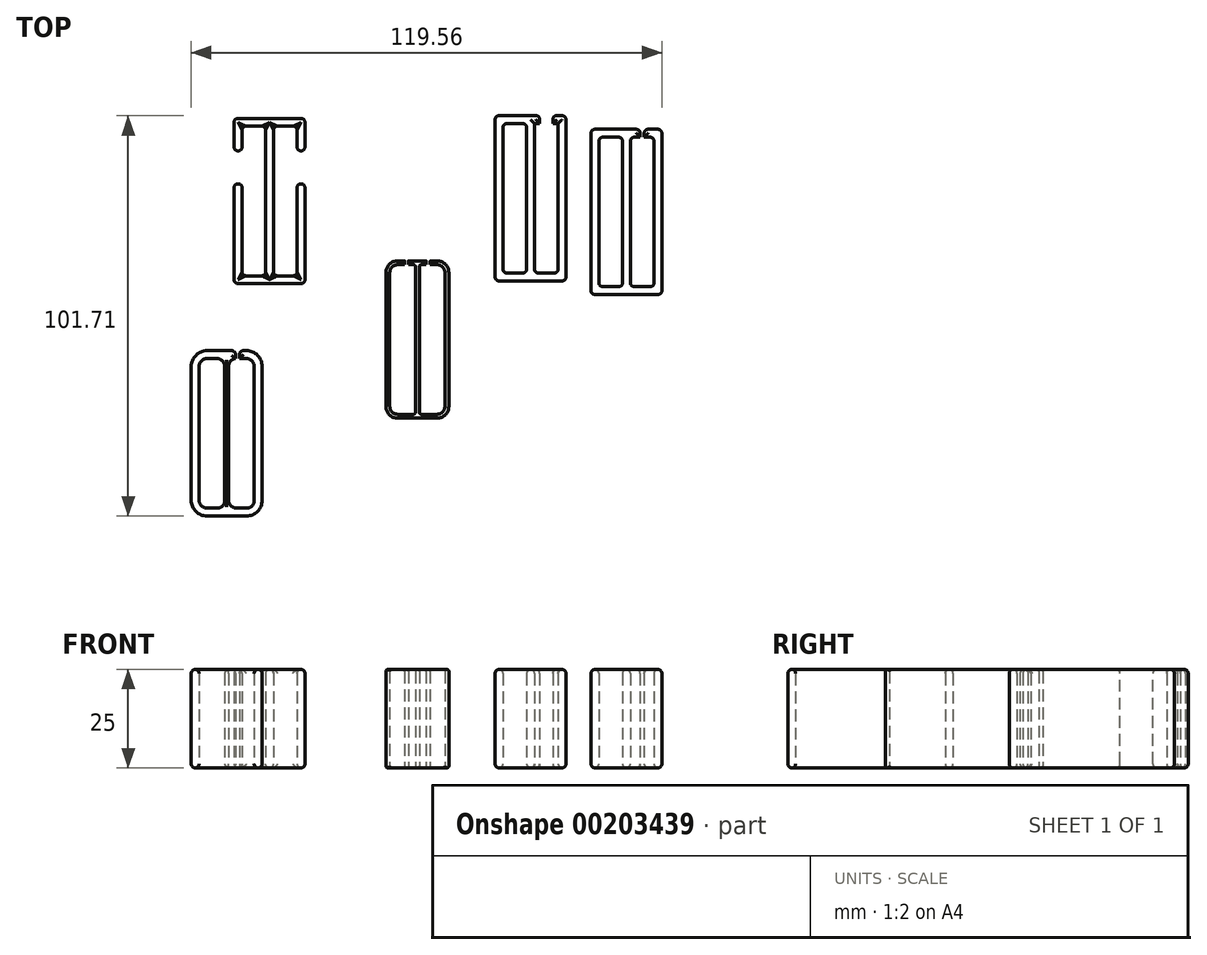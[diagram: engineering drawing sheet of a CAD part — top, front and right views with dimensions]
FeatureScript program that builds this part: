
annotation { "Feature Type Name" : "Feature", "Feature Type Description" : "" }
export const myFeature = defineFeature(function(context is Context, id is Id, definition is map)
    precondition{}
    {
        {
            var Q0;
            Q0=qCreatedBy(makeId("Top.planeOp"),FACE);
            var sketch = newSketch(context, id + "F0", { "sketchPlane" : qUnion([Q0])});
            skLineSegment(sketch, "E0", {"start": v(-46.96, 45) * mm, "end": v(-46.96, 53.26) * mm});
            skLineSegment(sketch, "E1", {"start": v(-46.96, 53.26) * mm, "end": v(-28.96, 53.26) * mm});
            skLineSegment(sketch, "E2", {"start": v(-28.96, 53.26) * mm, "end": v(-28.96, 45) * mm});
            skLineSegment(sketch, "E3", {"start": v(-37.96, 53.26) * mm, "end": v(-37.96, 11.26) * mm});
            skLineSegment(sketch, "E4", {"start": v(-37.96, 11.26) * mm, "end": v(-46.96, 11.26) * mm});
            skLineSegment(sketch, "E5", {"start": v(-46.96, 11.26) * mm, "end": v(-46.96, 36.63) * mm});
            skLineSegment(sketch, "E6", {"start": v(-37.96, 11.26) * mm, "end": v(-28.96, 11.26) * mm});
            skLineSegment(sketch, "E7", {"start": v(-28.96, 11.26) * mm, "end": v(-28.96, 36.63) * mm});
            skLineSegment(sketch, "E8.0", {"start": v(-30.96, 51.26) * mm, "end": v(-30.96, 45) * mm});
            skLineSegment(sketch, "E8.1", {"start": v(-44.96, 51.26) * mm, "end": v(-30.96, 51.26) * mm});
            skLineSegment(sketch, "E8.2", {"start": v(-44.96, 45) * mm, "end": v(-44.96, 51.26) * mm});
            skLineSegment(sketch, "E9.0", {"start": v(-44.96, 13.26) * mm, "end": v(-44.96, 36.63) * mm});
            skLineSegment(sketch, "E9.1", {"start": v(-40.12, 13.26) * mm, "end": v(-44.96, 13.26) * mm});
            skLineSegment(sketch, "E9.2", {"start": v(-40.12, 13.26) * mm, "end": v(-30.96, 13.26) * mm});
            skLineSegment(sketch, "E9.3", {"start": v(-30.96, 13.26) * mm, "end": v(-30.96, 36.63) * mm});
            skLineSegment(sketch, "E10.0", {"start": v(-38.96, 53.26) * mm, "end": v(-38.96, 11.26) * mm});
            skLineSegment(sketch, "E11.0", {"start": v(-36.96, 53.26) * mm, "end": v(-36.96, 11.26) * mm});
            skLineSegment(sketch, "E12", {"start": v(-46.96, 45) * mm, "end": v(-44.96, 45) * mm});
            skLineSegment(sketch, "E13", {"start": v(-30.96, 45) * mm, "end": v(-28.96, 45) * mm});
            skLineSegment(sketch, "E14", {"start": v(-30.96, 36.63) * mm, "end": v(-28.96, 36.63) * mm});
            skLineSegment(sketch, "E15", {"start": v(-46.96, 36.63) * mm, "end": v(-44.96, 36.63) * mm});
            skSolve(sketch);
        }
        {
            var Q0;
            {var subQ1=sQuery(id+"F0.wireOp",EDGE,"E5");Q0=makeQuery(id+"F0.imprint","IMPRINT",FACE,{"disambiguationData":[TD([[makeQuery(id+"F0.imprint","IMPRINT",EDGE,{"derivedFrom":subQ1}),-1.0]])]});}
            var Q1;
            {var subQ3=sQuery(id+"F0.wireOp",EDGE,"E9.2");var subQ5=sQuery(id+"F0.wireOp",EDGE,"E10.0");var subQ7=makeQuery(id+"F0.imprint","INTERSECT",VERTEX,{"derivedFrom":[subQ3,subQ5]});Q1=makeQuery(id+"F0.imprint","IMPRINT",FACE,{"disambiguationData":[TD([[makeQuery(id+"F0.imprint","IMPRINT",EDGE,{"disambiguationData":[TD([[subQ7,-1.0]])],"derivedFrom":subQ3}),-1.0]])]});}
            var Q2;
            {var subQ3=sQuery(id+"F0.wireOp",EDGE,"E9.2");var subQ5=sQuery(id+"F0.wireOp",EDGE,"E11.0");var subQ7=makeQuery(id+"F0.imprint","INTERSECT",VERTEX,{"derivedFrom":[subQ3,subQ5]});Q2=makeQuery(id+"F0.imprint","IMPRINT",FACE,{"disambiguationData":[TD([[makeQuery(id+"F0.imprint","IMPRINT",EDGE,{"disambiguationData":[TD([[subQ7,1.0]])],"derivedFrom":subQ3}),-1.0]])]});}
            var Q3;
            {var subQ4=sQuery(id+"F0.wireOp",EDGE,"E7");Q3=makeQuery(id+"F0.imprint","IMPRINT",FACE,{"disambiguationData":[TD([[makeQuery(id+"F0.imprint","IMPRINT",EDGE,{"derivedFrom":subQ4}),1.0]])]});}
            var Q4;
            {var subQ0=sQuery(id+"F0.wireOp",EDGE,"E8.1");var subQ1=sQuery(id+"F0.wireOp",EDGE,"E3");var subQ2=makeQuery(id+"F0.imprint","INTERSECT",VERTEX,{"derivedFrom":[subQ1,subQ0]});Q4=makeQuery(id+"F0.imprint","IMPRINT",FACE,{"disambiguationData":[TD([[makeQuery(id+"F0.imprint","IMPRINT",EDGE,{"disambiguationData":[TD([[subQ2,-1.0]])],"derivedFrom":subQ1}),-1.0]])]});}
            var Q5;
            {var subQ0=sQuery(id+"F0.wireOp",EDGE,"E8.1");var subQ1=sQuery(id+"F0.wireOp",EDGE,"E3");var subQ2=makeQuery(id+"F0.imprint","INTERSECT",VERTEX,{"derivedFrom":[subQ1,subQ0]});Q5=makeQuery(id+"F0.imprint","IMPRINT",FACE,{"disambiguationData":[TD([[makeQuery(id+"F0.imprint","IMPRINT",EDGE,{"disambiguationData":[TD([[subQ2,-1.0]])],"derivedFrom":subQ1}),1.0]])]});}
            var Q6;
            {var subQ5=sQuery(id+"F0.wireOp",EDGE,"E0");Q6=makeQuery(id+"F0.imprint","IMPRINT",FACE,{"disambiguationData":[TD([[makeQuery(id+"F0.imprint","IMPRINT",EDGE,{"derivedFrom":subQ5}),-1.0]])]});}
            var Q7;
            {var subQ1=sQuery(id+"F0.wireOp",EDGE,"E2");Q7=makeQuery(id+"F0.imprint","IMPRINT",FACE,{"disambiguationData":[TD([[makeQuery(id+"F0.imprint","IMPRINT",EDGE,{"derivedFrom":subQ1}),-1.0]])]});}
            var Q8;
            {var subQ0=sQuery(id+"F0.wireOp",EDGE,"E3");var subQ1=sQuery(id+"F0.wireOp",EDGE,"E1");var subQ2=makeQuery(id+"F0.imprint","INTERSECT",VERTEX,{"derivedFrom":[subQ1,subQ0]});Q8=makeQuery(id+"F0.imprint","IMPRINT",FACE,{"disambiguationData":[TD([[makeQuery(id+"F0.imprint","IMPRINT",EDGE,{"disambiguationData":[TD([[subQ2,1.0]])],"derivedFrom":subQ1}),-1.0]])]});}
            var Q9;
            {var subQ0=sQuery(id+"F0.wireOp",EDGE,"E3");var subQ1=sQuery(id+"F0.wireOp",EDGE,"E1");var subQ2=makeQuery(id+"F0.imprint","INTERSECT",VERTEX,{"derivedFrom":[subQ1,subQ0]});Q9=makeQuery(id+"F0.imprint","IMPRINT",FACE,{"disambiguationData":[TD([[makeQuery(id+"F0.imprint","IMPRINT",EDGE,{"disambiguationData":[TD([[subQ2,-1.0]])],"derivedFrom":subQ1}),-1.0]])]});}
            extrude(context, id + "F1", {"entities" : qUnion([Q0, Q1, Q2, Q3, Q4, Q5, Q6, Q7, Q8, Q9]), "depth" : 25 * mm, "offsetDistance" : 25 * mm});
        }
        {
            var Q0;
            Q0=makeQuery(id+"F1.opExtrude","SWEPT_FACE",FACE,{"disambiguationData":[OSD([sQuery(id+"F0.wireOp",EDGE,"E12")])]});
            var Q1;
            Q1=makeQuery(id+"F1.opExtrude","SWEPT_FACE",FACE,{"disambiguationData":[OSD([sQuery(id+"F0.wireOp",EDGE,"E13")])]});
            var Q2;
            Q2=makeQuery(id+"F1.opExtrude","SWEPT_FACE",FACE,{"disambiguationData":[OSD([sQuery(id+"F0.wireOp",EDGE,"E15")])]});
            var Q3;
            Q3=makeQuery(id+"F1.opExtrude","SWEPT_FACE",FACE,{"disambiguationData":[OSD([sQuery(id+"F0.wireOp",EDGE,"E14")])]});
            var Q4;
            Q4=makeQuery(id+"F1.opExtrude","CAP_FACE",FACE,{"disambiguationData":[OSD([sQuery(id+"F0.wireOp",EDGE,"E0"),sQuery(id+"F0.wireOp",EDGE,"E1"),sQuery(id+"F0.wireOp",EDGE,"E2"),sQuery(id+"F0.wireOp",EDGE,"E4"),sQuery(id+"F0.wireOp",EDGE,"E5"),sQuery(id+"F0.wireOp",EDGE,"E6"),sQuery(id+"F0.wireOp",EDGE,"E7"),sQuery(id+"F0.wireOp",EDGE,"E8.0"),sQuery(id+"F0.wireOp",EDGE,"E8.1"),sQuery(id+"F0.wireOp",EDGE,"E8.2"),sQuery(id+"F0.wireOp",EDGE,"E9.0"),sQuery(id+"F0.wireOp",EDGE,"E9.1"),sQuery(id+"F0.wireOp",EDGE,"E9.2"),sQuery(id+"F0.wireOp",EDGE,"E9.3"),sQuery(id+"F0.wireOp",EDGE,"E10.0"),sQuery(id+"F0.wireOp",EDGE,"E11.0"),sQuery(id+"F0.wireOp",EDGE,"E12"),sQuery(id+"F0.wireOp",EDGE,"E13"),sQuery(id+"F0.wireOp",EDGE,"E14"),sQuery(id+"F0.wireOp",EDGE,"E15")])],"isStart":false});
            var Q5;
            Q5=makeQuery(id+"F1.opExtrude","CAP_FACE",FACE,{"disambiguationData":[OSD([sQuery(id+"F0.wireOp",EDGE,"E0"),sQuery(id+"F0.wireOp",EDGE,"E1"),sQuery(id+"F0.wireOp",EDGE,"E2"),sQuery(id+"F0.wireOp",EDGE,"E4"),sQuery(id+"F0.wireOp",EDGE,"E5"),sQuery(id+"F0.wireOp",EDGE,"E6"),sQuery(id+"F0.wireOp",EDGE,"E7"),sQuery(id+"F0.wireOp",EDGE,"E8.0"),sQuery(id+"F0.wireOp",EDGE,"E8.1"),sQuery(id+"F0.wireOp",EDGE,"E8.2"),sQuery(id+"F0.wireOp",EDGE,"E9.0"),sQuery(id+"F0.wireOp",EDGE,"E9.1"),sQuery(id+"F0.wireOp",EDGE,"E9.2"),sQuery(id+"F0.wireOp",EDGE,"E9.3"),sQuery(id+"F0.wireOp",EDGE,"E10.0"),sQuery(id+"F0.wireOp",EDGE,"E11.0"),sQuery(id+"F0.wireOp",EDGE,"E12"),sQuery(id+"F0.wireOp",EDGE,"E13"),sQuery(id+"F0.wireOp",EDGE,"E14"),sQuery(id+"F0.wireOp",EDGE,"E15")])],"isStart":true});
            var Q6;
            Q6=makeQuery(id+"F1.opExtrude","SWEPT_EDGE",EDGE,{"disambiguationData":[OSD([sQuery(id+"F0.wireOp",EDGE,"E1"),sQuery(id+"F0.wireOp",EDGE,"E2")])]});
            var Q7;
            Q7=makeQuery(id+"F1.opExtrude","SWEPT_EDGE",EDGE,{"disambiguationData":[OSD([sQuery(id+"F0.wireOp",EDGE,"E0"),sQuery(id+"F0.wireOp",EDGE,"E1")])]});
            var Q8;
            Q8=makeQuery(id+"F1.opExtrude","SWEPT_EDGE",EDGE,{"disambiguationData":[OSD([sQuery(id+"F0.wireOp",EDGE,"E6"),sQuery(id+"F0.wireOp",EDGE,"E7")])]});
            var Q9;
            Q9=makeQuery(id+"F1.opExtrude","SWEPT_EDGE",EDGE,{"disambiguationData":[OSD([sQuery(id+"F0.wireOp",EDGE,"E4"),sQuery(id+"F0.wireOp",EDGE,"E5")])]});
            fillet(context, id + "F2", {"entities" : qUnion([Q0, Q1, Q2, Q3, Q4, Q5, Q6, Q7, Q8, Q9]), "radius" : 1 * mm, "tangentPropagation" : true, "allowEdgeOverflow" : false});
        }
        {
            var Q0;
            Q0=makeQuery(id+"F1.opExtrude","SWEPT_EDGE",EDGE,{"disambiguationData":[OSD([sQuery(id+"F0.wireOp",EDGE,"E8.1"),sQuery(id+"F0.wireOp",EDGE,"E10.0")])]});
            var Q1;
            Q1=makeQuery(id+"F1.opExtrude","SWEPT_EDGE",EDGE,{"disambiguationData":[OSD([sQuery(id+"F0.wireOp",EDGE,"E8.1"),sQuery(id+"F0.wireOp",EDGE,"E11.0")])]});
            var Q2;
            Q2=makeQuery(id+"F1.opExtrude","SWEPT_EDGE",EDGE,{"disambiguationData":[OSD([sQuery(id+"F0.wireOp",EDGE,"E8.1"),sQuery(id+"F0.wireOp",EDGE,"E8.2")])]});
            var Q3;
            Q3=makeQuery(id+"F1.opExtrude","SWEPT_EDGE",EDGE,{"disambiguationData":[OSD([sQuery(id+"F0.wireOp",EDGE,"E8.0"),sQuery(id+"F0.wireOp",EDGE,"E8.1")])]});
            var Q4;
            Q4=makeQuery(id+"F1.opExtrude","SWEPT_EDGE",EDGE,{"disambiguationData":[OSD([sQuery(id+"F0.wireOp",EDGE,"E9.2"),sQuery(id+"F0.wireOp",EDGE,"E9.3")])]});
            var Q5;
            Q5=makeQuery(id+"F1.opExtrude","SWEPT_EDGE",EDGE,{"disambiguationData":[OSD([sQuery(id+"F0.wireOp",EDGE,"E9.2"),sQuery(id+"F0.wireOp",EDGE,"E10.0")])]});
            var Q6;
            Q6=makeQuery(id+"F1.opExtrude","SWEPT_EDGE",EDGE,{"disambiguationData":[OSD([sQuery(id+"F0.wireOp",EDGE,"E9.2"),sQuery(id+"F0.wireOp",EDGE,"E11.0")])]});
            var Q7;
            Q7=makeQuery(id+"F1.opExtrude","SWEPT_EDGE",EDGE,{"disambiguationData":[OSD([sQuery(id+"F0.wireOp",EDGE,"E9.0"),sQuery(id+"F0.wireOp",EDGE,"E9.1")])]});
            fillet(context, id + "F3", {"entities" : qUnion([Q0, Q1, Q2, Q3, Q4, Q5, Q6, Q7]), "radius" : 1 * mm, "tangentPropagation" : true, "allowEdgeOverflow" : false});
        }
        {
            var Q0;
            Q0=qCreatedBy(makeId("Top.planeOp"),FACE);
            var sketch = newSketch(context, id + "F4", { "sketchPlane" : qUnion([Q0])});
            skLineSegment(sketch, "E16.bottom", {"start": v(19.35, 53.95) * mm, "end": v(28.35, 53.95) * mm});
            skLineSegment(sketch, "E16.top", {"start": v(19.35, 11.95) * mm, "end": v(28.35, 11.95) * mm});
            skLineSegment(sketch, "E16.left", {"start": v(19.35, 53.95) * mm, "end": v(19.35, 11.95) * mm});
            skLineSegment(sketch, "E16.right", {"start": v(28.35, 53.95) * mm, "end": v(28.35, 11.95) * mm});
            skLineSegment(sketch, "E17.bottom", {"start": v(28.35, 53.95) * mm, "end": v(30.68, 53.95) * mm});
            skLineSegment(sketch, "E17.top", {"start": v(28.35, 11.95) * mm, "end": v(37.35, 11.95) * mm});
            skLineSegment(sketch, "E17.right", {"start": v(37.35, 53.95) * mm, "end": v(37.35, 11.95) * mm});
            skLineSegment(sketch, "E18", {"start": v(34.01, 53.95) * mm, "end": v(37.35, 53.95) * mm});
            skLineSegment(sketch, "E19.0", {"start": v(21.35, 51.95) * mm, "end": v(27.35, 51.95) * mm});
            skLineSegment(sketch, "E19.1", {"start": v(21.35, 51.95) * mm, "end": v(21.35, 13.95) * mm});
            skLineSegment(sketch, "E19.2", {"start": v(21.35, 13.95) * mm, "end": v(27.35, 13.95) * mm});
            skLineSegment(sketch, "E20.0", {"start": v(29.35, 51.95) * mm, "end": v(30.68, 51.95) * mm});
            skLineSegment(sketch, "E20.1", {"start": v(34.01, 51.95) * mm, "end": v(35.35, 51.95) * mm});
            skLineSegment(sketch, "E20.2", {"start": v(35.35, 51.95) * mm, "end": v(35.35, 13.95) * mm});
            skLineSegment(sketch, "E20.3", {"start": v(29.35, 13.95) * mm, "end": v(35.35, 13.95) * mm});
            skLineSegment(sketch, "E21", {"start": v(30.68, 53.95) * mm, "end": v(30.68, 51.95) * mm});
            skLineSegment(sketch, "E22", {"start": v(34.01, 53.95) * mm, "end": v(34.01, 51.95) * mm});
            skLineSegment(sketch, "E23.0", {"start": v(27.35, 52.61) * mm, "end": v(27.35, 10.61) * mm});
            skLineSegment(sketch, "E24.MirrorCS", {"start": v(29.35, 52.61) * mm, "end": v(29.35, 10.61) * mm});
            skSolve(sketch);
        }
        {
            var Q0;
            {var subQ0=sQuery(id+"F4.wireOp",EDGE,"E16.left");Q0=makeQuery(id+"F4.imprint","IMPRINT",FACE,{"disambiguationData":[TD([[makeQuery(id+"F4.imprint","IMPRINT",EDGE,{"derivedFrom":subQ0}),1.0]])]});}
            var Q1;
            {var subQ0=sQuery(id+"F4.wireOp",EDGE,"E16.right");Q1=makeQuery(id+"F4.imprint","IMPRINT",FACE,{"disambiguationData":[TD([[makeQuery(id+"F4.imprint","IMPRINT",EDGE,{"derivedFrom":subQ0}),-1.0]])]});}
            var Q2;
            {var subQ4=sQuery(id+"F4.wireOp",EDGE,"E16.right");Q2=makeQuery(id+"F4.imprint","IMPRINT",FACE,{"disambiguationData":[TD([[makeQuery(id+"F4.imprint","IMPRINT",EDGE,{"derivedFrom":subQ4}),1.0]])]});}
            var Q3;
            {var subQ4=sQuery(id+"F4.wireOp",EDGE,"E20.0");Q3=makeQuery(id+"F4.imprint","IMPRINT",FACE,{"disambiguationData":[TD([[makeQuery(id+"F4.imprint","IMPRINT",EDGE,{"derivedFrom":subQ4}),1.0]])]});}
            var Q4;
            {var subQ0=sQuery(id+"F4.wireOp",EDGE,"E17.right");Q4=makeQuery(id+"F4.imprint","IMPRINT",FACE,{"disambiguationData":[TD([[makeQuery(id+"F4.imprint","IMPRINT",EDGE,{"derivedFrom":subQ0}),-1.0]])]});}
            extrude(context, id + "F5", {"entities" : qUnion([Q0, Q1, Q2, Q3, Q4]), "depth" : 25 * mm, "offsetDistance" : 25 * mm});
        }
        {
            var Q0;
            Q0=makeQuery(id+"F5.opExtrude","CAP_FACE",FACE,{"disambiguationData":[OSD([sQuery(id+"F4.wireOp",EDGE,"E16.bottom"),sQuery(id+"F4.wireOp",EDGE,"E16.top"),sQuery(id+"F4.wireOp",EDGE,"E16.left"),sQuery(id+"F4.wireOp",EDGE,"E17.bottom"),sQuery(id+"F4.wireOp",EDGE,"E17.top"),sQuery(id+"F4.wireOp",EDGE,"E17.right"),sQuery(id+"F4.wireOp",EDGE,"E18"),sQuery(id+"F4.wireOp",EDGE,"E19.0"),sQuery(id+"F4.wireOp",EDGE,"E19.1"),sQuery(id+"F4.wireOp",EDGE,"E19.2"),sQuery(id+"F4.wireOp",EDGE,"E20.0"),sQuery(id+"F4.wireOp",EDGE,"E20.1"),sQuery(id+"F4.wireOp",EDGE,"E20.2"),sQuery(id+"F4.wireOp",EDGE,"E20.3"),sQuery(id+"F4.wireOp",EDGE,"E21"),sQuery(id+"F4.wireOp",EDGE,"E22"),sQuery(id+"F4.wireOp",EDGE,"E23.0"),sQuery(id+"F4.wireOp",EDGE,"E24.MirrorCS")])],"isStart":false});
            var Q1;
            Q1=makeQuery(id+"F5.opExtrude","CAP_FACE",FACE,{"disambiguationData":[OSD([sQuery(id+"F4.wireOp",EDGE,"E16.bottom"),sQuery(id+"F4.wireOp",EDGE,"E16.top"),sQuery(id+"F4.wireOp",EDGE,"E16.left"),sQuery(id+"F4.wireOp",EDGE,"E17.bottom"),sQuery(id+"F4.wireOp",EDGE,"E17.top"),sQuery(id+"F4.wireOp",EDGE,"E17.right"),sQuery(id+"F4.wireOp",EDGE,"E18"),sQuery(id+"F4.wireOp",EDGE,"E19.0"),sQuery(id+"F4.wireOp",EDGE,"E19.1"),sQuery(id+"F4.wireOp",EDGE,"E19.2"),sQuery(id+"F4.wireOp",EDGE,"E20.0"),sQuery(id+"F4.wireOp",EDGE,"E20.1"),sQuery(id+"F4.wireOp",EDGE,"E20.2"),sQuery(id+"F4.wireOp",EDGE,"E20.3"),sQuery(id+"F4.wireOp",EDGE,"E21"),sQuery(id+"F4.wireOp",EDGE,"E22"),sQuery(id+"F4.wireOp",EDGE,"E23.0"),sQuery(id+"F4.wireOp",EDGE,"E24.MirrorCS")])],"isStart":true});
            var Q2;
            Q2=makeQuery(id+"F5.opExtrude","SWEPT_EDGE",EDGE,{"disambiguationData":[OSD([sQuery(id+"F4.wireOp",EDGE,"E19.0"),sQuery(id+"F4.wireOp",EDGE,"E19.1")])]});
            var Q3;
            Q3=makeQuery(id+"F5.opExtrude","SWEPT_EDGE",EDGE,{"disambiguationData":[OSD([sQuery(id+"F4.wireOp",EDGE,"E19.0"),sQuery(id+"F4.wireOp",EDGE,"E23.0")])]});
            var Q4;
            Q4=makeQuery(id+"F5.opExtrude","SWEPT_EDGE",EDGE,{"disambiguationData":[OSD([sQuery(id+"F4.wireOp",EDGE,"E19.1"),sQuery(id+"F4.wireOp",EDGE,"E19.2")])]});
            var Q5;
            Q5=makeQuery(id+"F5.opExtrude","SWEPT_EDGE",EDGE,{"disambiguationData":[OSD([sQuery(id+"F4.wireOp",EDGE,"E20.3"),sQuery(id+"F4.wireOp",EDGE,"E24.MirrorCS")])]});
            var Q6;
            Q6=makeQuery(id+"F5.opExtrude","SWEPT_EDGE",EDGE,{"disambiguationData":[OSD([sQuery(id+"F4.wireOp",EDGE,"E19.2"),sQuery(id+"F4.wireOp",EDGE,"E23.0")])]});
            var Q7;
            Q7=makeQuery(id+"F5.opExtrude","SWEPT_EDGE",EDGE,{"disambiguationData":[OSD([sQuery(id+"F4.wireOp",EDGE,"E20.2"),sQuery(id+"F4.wireOp",EDGE,"E20.3")])]});
            var Q8;
            Q8=makeQuery(id+"F5.opExtrude","SWEPT_EDGE",EDGE,{"disambiguationData":[OSD([sQuery(id+"F4.wireOp",EDGE,"E16.bottom"),sQuery(id+"F4.wireOp",EDGE,"E16.left")])]});
            var Q9;
            Q9=makeQuery(id+"F5.opExtrude","SWEPT_EDGE",EDGE,{"disambiguationData":[OSD([sQuery(id+"F4.wireOp",EDGE,"E17.right"),sQuery(id+"F4.wireOp",EDGE,"E18")])]});
            var Q10;
            Q10=makeQuery(id+"F5.opExtrude","SWEPT_EDGE",EDGE,{"disambiguationData":[OSD([sQuery(id+"F4.wireOp",EDGE,"E17.top"),sQuery(id+"F4.wireOp",EDGE,"E17.right")])]});
            var Q11;
            Q11=makeQuery(id+"F5.opExtrude","SWEPT_EDGE",EDGE,{"disambiguationData":[OSD([sQuery(id+"F4.wireOp",EDGE,"E16.top"),sQuery(id+"F4.wireOp",EDGE,"E16.left")])]});
            var Q12;
            Q12=makeQuery(id+"F5.opExtrude","SWEPT_EDGE",EDGE,{"disambiguationData":[OSD([sQuery(id+"F4.wireOp",EDGE,"E17.bottom"),sQuery(id+"F4.wireOp",EDGE,"E21")])]});
            var Q13;
            Q13=makeQuery(id+"F5.opExtrude","SWEPT_EDGE",EDGE,{"disambiguationData":[OSD([sQuery(id+"F4.wireOp",EDGE,"E18"),sQuery(id+"F4.wireOp",EDGE,"E22")])]});
            fillet(context, id + "F6", {"entities" : qUnion([Q0, Q1, Q2, Q3, Q4, Q5, Q6, Q7, Q8, Q9, Q10, Q11, Q12, Q13]), "radius" : 1 * mm, "tangentPropagation" : true, "allowEdgeOverflow" : false});
        }
        {
            var Q0;
            Q0=qCreatedBy(makeId("Top.planeOp"),FACE);
            var sketch = newSketch(context, id + "F7", { "sketchPlane" : qUnion([Q0])});
            skLineSegment(sketch, "E25.bottom", {"start": v(43.7, 50.48) * mm, "end": v(52.7, 50.48) * mm});
            skLineSegment(sketch, "E25.top", {"start": v(43.7, 8.48) * mm, "end": v(52.7, 8.48) * mm});
            skLineSegment(sketch, "E25.left", {"start": v(43.7, 50.48) * mm, "end": v(43.7, 8.48) * mm});
            skLineSegment(sketch, "E25.right", {"start": v(61.7, 50.48) * mm, "end": v(61.7, 8.48) * mm});
            skLineSegment(sketch, "E26", {"start": v(52.7, 50.48) * mm, "end": v(61.7, 50.48) * mm});
            skLineSegment(sketch, "E27", {"start": v(52.7, 8.48) * mm, "end": v(61.7, 8.48) * mm});
            skLineSegment(sketch, "E28.0", {"start": v(45.7, 48.48) * mm, "end": v(45.7, 10.48) * mm});
            skLineSegment(sketch, "E28.1", {"start": v(52.7, 48.48) * mm, "end": v(53.7, 48.48) * mm});
            skLineSegment(sketch, "E28.2", {"start": v(59.7, 48.48) * mm, "end": v(59.7, 10.48) * mm});
            skLineSegment(sketch, "E28.3", {"start": v(45.7, 48.48) * mm, "end": v(52.7, 48.48) * mm});
            skLineSegment(sketch, "E28.4", {"start": v(52.7, 10.48) * mm, "end": v(59.7, 10.48) * mm});
            skLineSegment(sketch, "E28.5", {"start": v(45.7, 10.48) * mm, "end": v(52.7, 10.48) * mm});
            skLineSegment(sketch, "E29", {"start": v(52.7, 48.48) * mm, "end": v(52.7, 10.48) * mm});
            skLineSegment(sketch, "E30.0", {"start": v(51.7, 48.48) * mm, "end": v(51.7, 10.48) * mm});
            skLineSegment(sketch, "E31.MirrorCS", {"start": v(53.7, 48.48) * mm, "end": v(53.7, 10.48) * mm});
            skLineSegment(sketch, "E32", {"start": v(53.7, 48.48) * mm, "end": v(59.7, 48.48) * mm});
            skLineSegment(sketch, "E33", {"start": v(56.7, 48.48) * mm, "end": v(56.7, 50.48) * mm});
            skLineSegment(sketch, "E34.0", {"start": v(57.2, 48.48) * mm, "end": v(57.2, 50.48) * mm});
            skLineSegment(sketch, "E35.MirrorCS", {"start": v(56.2, 48.48) * mm, "end": v(56.2, 50.48) * mm});
            skSolve(sketch);
        }
        {
            var Q0;
            {var subQ5=sQuery(id+"F7.wireOp",EDGE,"E25.bottom");Q0=makeQuery(id+"F7.imprint","IMPRINT",FACE,{"disambiguationData":[TD([[makeQuery(id+"F7.imprint","IMPRINT",EDGE,{"derivedFrom":subQ5}),-1.0]])]});}
            var Q1;
            {var subQ0=sQuery(id+"F7.wireOp",EDGE,"E29");Q1=makeQuery(id+"F7.imprint","IMPRINT",FACE,{"disambiguationData":[TD([[makeQuery(id+"F7.imprint","IMPRINT",EDGE,{"derivedFrom":subQ0}),-1.0]])]});}
            var Q2;
            Q2=makeQuery(id+"F7.imprint","IMPRINT",FACE,{"disambiguationData":[TD([[makeQuery(id+"F7.imprint","IMPRINT",EDGE,{"derivedFrom":sQuery(id+"F7.wireOp",EDGE,"E28.1")}),-1.0]])]});
            extrude(context, id + "F8", {"entities" : qUnion([Q0, Q1, Q2]), "depth" : 25 * mm, "offsetDistance" : 25 * mm});
        }
        {
            var Q0;
            Q0=makeQuery(id+"F8.opExtrude","CAP_FACE",FACE,{"disambiguationData":[OSD([sQuery(id+"F7.wireOp",EDGE,"E25.bottom"),sQuery(id+"F7.wireOp",EDGE,"E25.top"),sQuery(id+"F7.wireOp",EDGE,"E25.left"),sQuery(id+"F7.wireOp",EDGE,"E25.right"),sQuery(id+"F7.wireOp",EDGE,"E26"),sQuery(id+"F7.wireOp",EDGE,"E27"),sQuery(id+"F7.wireOp",EDGE,"E28.0"),sQuery(id+"F7.wireOp",EDGE,"E28.2"),sQuery(id+"F7.wireOp",EDGE,"E28.3"),sQuery(id+"F7.wireOp",EDGE,"E28.4"),sQuery(id+"F7.wireOp",EDGE,"E28.5"),sQuery(id+"F7.wireOp",EDGE,"E30.0"),sQuery(id+"F7.wireOp",EDGE,"E31.MirrorCS"),sQuery(id+"F7.wireOp",EDGE,"E32"),sQuery(id+"F7.wireOp",EDGE,"E34.0"),sQuery(id+"F7.wireOp",EDGE,"E35.MirrorCS")])],"isStart":false});
            var Q1;
            Q1=makeQuery(id+"F8.opExtrude","CAP_FACE",FACE,{"disambiguationData":[OSD([sQuery(id+"F7.wireOp",EDGE,"E25.bottom"),sQuery(id+"F7.wireOp",EDGE,"E25.top"),sQuery(id+"F7.wireOp",EDGE,"E25.left"),sQuery(id+"F7.wireOp",EDGE,"E25.right"),sQuery(id+"F7.wireOp",EDGE,"E26"),sQuery(id+"F7.wireOp",EDGE,"E27"),sQuery(id+"F7.wireOp",EDGE,"E28.0"),sQuery(id+"F7.wireOp",EDGE,"E28.2"),sQuery(id+"F7.wireOp",EDGE,"E28.3"),sQuery(id+"F7.wireOp",EDGE,"E28.4"),sQuery(id+"F7.wireOp",EDGE,"E28.5"),sQuery(id+"F7.wireOp",EDGE,"E30.0"),sQuery(id+"F7.wireOp",EDGE,"E31.MirrorCS"),sQuery(id+"F7.wireOp",EDGE,"E32"),sQuery(id+"F7.wireOp",EDGE,"E34.0"),sQuery(id+"F7.wireOp",EDGE,"E35.MirrorCS")])],"isStart":true});
            var Q2;
            Q2=makeQuery(id+"F8.opExtrude","SWEPT_EDGE",EDGE,{"disambiguationData":[OSD([sQuery(id+"F7.wireOp",EDGE,"E25.right"),sQuery(id+"F7.wireOp",EDGE,"E26")])]});
            var Q3;
            Q3=makeQuery(id+"F8.opExtrude","SWEPT_EDGE",EDGE,{"disambiguationData":[OSD([sQuery(id+"F7.wireOp",EDGE,"E25.bottom"),sQuery(id+"F7.wireOp",EDGE,"E25.left")])]});
            var Q4;
            Q4=makeQuery(id+"F8.opExtrude","SWEPT_EDGE",EDGE,{"disambiguationData":[OSD([sQuery(id+"F7.wireOp",EDGE,"E25.right"),sQuery(id+"F7.wireOp",EDGE,"E27")])]});
            var Q5;
            Q5=makeQuery(id+"F8.opExtrude","SWEPT_EDGE",EDGE,{"disambiguationData":[OSD([sQuery(id+"F7.wireOp",EDGE,"E25.top"),sQuery(id+"F7.wireOp",EDGE,"E25.left")])]});
            var Q6;
            Q6=makeQuery(id+"F8.opExtrude","SWEPT_EDGE",EDGE,{"disambiguationData":[OSD([sQuery(id+"F7.wireOp",EDGE,"E28.3"),sQuery(id+"F7.wireOp",EDGE,"E30.0")])]});
            var Q7;
            Q7=makeQuery(id+"F8.opExtrude","SWEPT_EDGE",EDGE,{"disambiguationData":[OSD([sQuery(id+"F7.wireOp",EDGE,"E28.0"),sQuery(id+"F7.wireOp",EDGE,"E28.3")])]});
            var Q8;
            Q8=makeQuery(id+"F8.opExtrude","SWEPT_EDGE",EDGE,{"disambiguationData":[OSD([sQuery(id+"F7.wireOp",EDGE,"E28.5"),sQuery(id+"F7.wireOp",EDGE,"E30.0")])]});
            var Q9;
            Q9=makeQuery(id+"F8.opExtrude","SWEPT_EDGE",EDGE,{"disambiguationData":[OSD([sQuery(id+"F7.wireOp",EDGE,"E28.2"),sQuery(id+"F7.wireOp",EDGE,"E28.4")])]});
            var Q10;
            Q10=makeQuery(id+"F8.opExtrude","SWEPT_EDGE",EDGE,{"disambiguationData":[OSD([sQuery(id+"F7.wireOp",EDGE,"E26"),sQuery(id+"F7.wireOp",EDGE,"E34.0")])]});
            var Q11;
            Q11=makeQuery(id+"F8.opExtrude","SWEPT_EDGE",EDGE,{"disambiguationData":[OSD([sQuery(id+"F7.wireOp",EDGE,"E26"),sQuery(id+"F7.wireOp",EDGE,"E35.MirrorCS")])]});
            var Q12;
            Q12=makeQuery(id+"F8.opExtrude","SWEPT_EDGE",EDGE,{"disambiguationData":[OSD([sQuery(id+"F7.wireOp",EDGE,"E28.4"),sQuery(id+"F7.wireOp",EDGE,"E31.MirrorCS")])]});
            var Q13;
            Q13=makeQuery(id+"F8.opExtrude","SWEPT_EDGE",EDGE,{"disambiguationData":[OSD([sQuery(id+"F7.wireOp",EDGE,"E28.0"),sQuery(id+"F7.wireOp",EDGE,"E28.5")])]});
            var Q14;
            Q14=makeQuery(id+"F8.opExtrude","SWEPT_EDGE",EDGE,{"disambiguationData":[OSD([sQuery(id+"F7.wireOp",EDGE,"E28.2"),sQuery(id+"F7.wireOp",EDGE,"E32")])]});
            var Q15;
            Q15=makeQuery(id+"F8.opExtrude","SWEPT_EDGE",EDGE,{"disambiguationData":[OSD([sQuery(id+"F7.wireOp",EDGE,"E28.1"),sQuery(id+"F7.wireOp",EDGE,"E31.MirrorCS"),sQuery(id+"F7.wireOp",EDGE,"E32")])]});
            fillet(context, id + "F9", {"entities" : qUnion([Q0, Q1, Q2, Q3, Q4, Q5, Q6, Q7, Q8, Q9, Q10, Q11, Q12, Q13, Q14, Q15]), "radius" : 1 * mm, "tangentPropagation" : true, "allowEdgeOverflow" : false});
        }
        {
            var Q0;
            Q0=qCreatedBy(makeId("Top.planeOp"),FACE);
            var sketch = newSketch(context, id + "F10", { "sketchPlane" : qUnion([Q0])});
            skLineSegment(sketch, "E36.bottom", {"start": v(-53.85, -7.76) * mm, "end": v(-43.85, -7.76) * mm});
            skLineSegment(sketch, "E36.top", {"start": v(-53.85, -45.76) * mm, "end": v(-43.85, -45.76) * mm});
            skLineSegment(sketch, "E36.left", {"start": v(-55.85, -9.76) * mm, "end": v(-55.85, -43.76) * mm});
            skLineSegment(sketch, "E36.right", {"start": v(-41.85, -9.76) * mm, "end": v(-41.85, -43.76) * mm});
            skPoint(sketch, "E37.visualSharp", {"position": v(-55.85, -7.76) * mm});
            skArc(sketch, "E37.filletArc", {"start": v(-53.85, -7.76) * mm, "mid": v(-55.27, -8.35) * mm, "end": v(-55.85, -9.76) * mm});
            skPoint(sketch, "E38.visualSharp", {"position": v(-55.85, -45.76) * mm});
            skArc(sketch, "E38.filletArc", {"start": v(-55.85, -43.76) * mm, "mid": v(-55.27, -45.18) * mm, "end": v(-53.85, -45.76) * mm});
            skPoint(sketch, "E39.visualSharp", {"position": v(-41.85, -45.76) * mm});
            skArc(sketch, "E39.filletArc", {"start": v(-43.85, -45.76) * mm, "mid": v(-42.44, -45.18) * mm, "end": v(-41.85, -43.76) * mm});
            skPoint(sketch, "E40.visualSharp", {"position": v(-41.85, -7.76) * mm});
            skArc(sketch, "E40.filletArc", {"start": v(-41.85, -9.76) * mm, "mid": v(-42.44, -8.35) * mm, "end": v(-43.85, -7.76) * mm});
            skArc(sketch, "E41.0", {"start": v(-53.85, -5.76) * mm, "mid": v(-56.68, -6.93) * mm, "end": v(-57.85, -9.76) * mm});
            skLineSegment(sketch, "E41.1", {"start": v(-53.85, -5.76) * mm, "end": v(-43.85, -5.76) * mm});
            skLineSegment(sketch, "E41.2", {"start": v(-57.85, -9.76) * mm, "end": v(-57.85, -43.76) * mm});
            skArc(sketch, "E41.3", {"start": v(-39.85, -9.76) * mm, "mid": v(-41.02, -6.93) * mm, "end": v(-43.85, -5.76) * mm});
            skArc(sketch, "E41.4", {"start": v(-57.85, -43.76) * mm, "mid": v(-56.68, -46.6) * mm, "end": v(-53.85, -47.76) * mm});
            skLineSegment(sketch, "E41.5", {"start": v(-53.85, -47.76) * mm, "end": v(-43.85, -47.76) * mm});
            skArc(sketch, "E41.6", {"start": v(-43.85, -47.76) * mm, "mid": v(-41.02, -46.6) * mm, "end": v(-39.85, -43.76) * mm});
            skLineSegment(sketch, "E41.7", {"start": v(-39.85, -9.76) * mm, "end": v(-39.85, -43.76) * mm});
            skLineSegment(sketch, "E42", {"start": v(-48.85, -7.76) * mm, "end": v(-48.85, -45.76) * mm});
            skLineSegment(sketch, "E43.0", {"start": v(-49.35, -7.76) * mm, "end": v(-49.35, -45.76) * mm});
            skLineSegment(sketch, "E44.MirrorCS", {"start": v(-48.35, -7.76) * mm, "end": v(-48.35, -45.76) * mm});
            skLineSegment(sketch, "E45", {"start": v(-48.35, -7.76) * mm, "end": v(-43.85, -7.76) * mm, "construction": true});
            skLineSegment(sketch, "E46", {"start": v(-46.1, -7.76) * mm, "end": v(-46.1, -5.76) * mm});
            skLineSegment(sketch, "E47.0", {"start": v(-45.6, -7.76) * mm, "end": v(-45.6, -5.76) * mm});
            skLineSegment(sketch, "E48.MirrorCS", {"start": v(-46.6, -7.76) * mm, "end": v(-46.6, -5.76) * mm});
            skSolve(sketch);
        }
        {
            var Q0;
            Q0=makeQuery(id+"F10.imprint","IMPRINT",FACE,{"disambiguationData":[TD([[makeQuery(id+"F10.imprint","IMPRINT",EDGE,{"derivedFrom":sQuery(id+"F10.wireOp",EDGE,"E36.left")}),-1.0]])]});
            var Q1;
            {var subQ0=sQuery(id+"F10.wireOp",EDGE,"E42");Q1=makeQuery(id+"F10.imprint","IMPRINT",FACE,{"disambiguationData":[TD([[makeQuery(id+"F10.imprint","IMPRINT",EDGE,{"derivedFrom":subQ0}),-1.0]])]});}
            var Q2;
            {var subQ0=sQuery(id+"F10.wireOp",EDGE,"E42");Q2=makeQuery(id+"F10.imprint","IMPRINT",FACE,{"disambiguationData":[TD([[makeQuery(id+"F10.imprint","IMPRINT",EDGE,{"derivedFrom":subQ0}),1.0]])]});}
            extrude(context, id + "F11", {"entities" : qUnion([Q0, Q1, Q2]), "depth" : 25 * mm, "offsetDistance" : 25 * mm});
        }
        {
            var Q0;
            Q0=makeQuery(id+"F11.opExtrude","SWEPT_EDGE",EDGE,{"disambiguationData":[OSD([sQuery(id+"F10.wireOp",EDGE,"E36.bottom"),sQuery(id+"F10.wireOp",EDGE,"E44.MirrorCS")])]});
            var Q1;
            Q1=makeQuery(id+"F11.opExtrude","SWEPT_EDGE",EDGE,{"disambiguationData":[OSD([sQuery(id+"F10.wireOp",EDGE,"E36.top"),sQuery(id+"F10.wireOp",EDGE,"E44.MirrorCS")])]});
            var Q2;
            Q2=makeQuery(id+"F11.opExtrude","SWEPT_EDGE",EDGE,{"disambiguationData":[OSD([sQuery(id+"F10.wireOp",EDGE,"E36.top"),sQuery(id+"F10.wireOp",EDGE,"E43.0")])]});
            var Q3;
            Q3=makeQuery(id+"F11.opExtrude","SWEPT_EDGE",EDGE,{"disambiguationData":[OSD([sQuery(id+"F10.wireOp",EDGE,"E36.bottom"),sQuery(id+"F10.wireOp",EDGE,"E43.0")])]});
            fillet(context, id + "F12", {"entities" : qUnion([Q0, Q1, Q2, Q3]), "radius" : 2 * mm, "tangentPropagation" : true, "allowEdgeOverflow" : false});
        }
        {
            var Q0;
            Q0=makeQuery(id+"F11.opExtrude","CAP_FACE",FACE,{"disambiguationData":[OSD([sQuery(id+"F10.wireOp",EDGE,"E36.bottom"),sQuery(id+"F10.wireOp",EDGE,"E36.top"),sQuery(id+"F10.wireOp",EDGE,"E36.left"),sQuery(id+"F10.wireOp",EDGE,"E36.right"),sQuery(id+"F10.wireOp",EDGE,"E37.filletArc"),sQuery(id+"F10.wireOp",EDGE,"E38.filletArc"),sQuery(id+"F10.wireOp",EDGE,"E39.filletArc"),sQuery(id+"F10.wireOp",EDGE,"E40.filletArc"),sQuery(id+"F10.wireOp",EDGE,"E41.0"),sQuery(id+"F10.wireOp",EDGE,"E41.1"),sQuery(id+"F10.wireOp",EDGE,"E41.2"),sQuery(id+"F10.wireOp",EDGE,"E41.3"),sQuery(id+"F10.wireOp",EDGE,"E41.4"),sQuery(id+"F10.wireOp",EDGE,"E41.5"),sQuery(id+"F10.wireOp",EDGE,"E41.6"),sQuery(id+"F10.wireOp",EDGE,"E41.7"),sQuery(id+"F10.wireOp",EDGE,"E43.0"),sQuery(id+"F10.wireOp",EDGE,"E44.MirrorCS"),sQuery(id+"F10.wireOp",EDGE,"E47.0"),sQuery(id+"F10.wireOp",EDGE,"E48.MirrorCS")])],"isStart":false});
            var Q1;
            Q1=makeQuery(id+"F11.opExtrude","SWEPT_EDGE",EDGE,{"disambiguationData":[OSD([sQuery(id+"F10.wireOp",EDGE,"E41.1"),sQuery(id+"F10.wireOp",EDGE,"E47.0")])]});
            var Q2;
            Q2=makeQuery(id+"F11.opExtrude","SWEPT_EDGE",EDGE,{"disambiguationData":[OSD([sQuery(id+"F10.wireOp",EDGE,"E41.1"),sQuery(id+"F10.wireOp",EDGE,"E48.MirrorCS")])]});
            var Q3;
            Q3=makeQuery(id+"F11.opExtrude","CAP_FACE",FACE,{"disambiguationData":[OSD([sQuery(id+"F10.wireOp",EDGE,"E36.bottom"),sQuery(id+"F10.wireOp",EDGE,"E36.top"),sQuery(id+"F10.wireOp",EDGE,"E36.left"),sQuery(id+"F10.wireOp",EDGE,"E36.right"),sQuery(id+"F10.wireOp",EDGE,"E37.filletArc"),sQuery(id+"F10.wireOp",EDGE,"E38.filletArc"),sQuery(id+"F10.wireOp",EDGE,"E39.filletArc"),sQuery(id+"F10.wireOp",EDGE,"E40.filletArc"),sQuery(id+"F10.wireOp",EDGE,"E41.0"),sQuery(id+"F10.wireOp",EDGE,"E41.1"),sQuery(id+"F10.wireOp",EDGE,"E41.2"),sQuery(id+"F10.wireOp",EDGE,"E41.3"),sQuery(id+"F10.wireOp",EDGE,"E41.4"),sQuery(id+"F10.wireOp",EDGE,"E41.5"),sQuery(id+"F10.wireOp",EDGE,"E41.6"),sQuery(id+"F10.wireOp",EDGE,"E41.7"),sQuery(id+"F10.wireOp",EDGE,"E43.0"),sQuery(id+"F10.wireOp",EDGE,"E44.MirrorCS"),sQuery(id+"F10.wireOp",EDGE,"E47.0"),sQuery(id+"F10.wireOp",EDGE,"E48.MirrorCS")])],"isStart":true});
            fillet(context, id + "F13", {"entities" : qUnion([Q0, Q1, Q2, Q3]), "radius" : 1 * mm, "tangentPropagation" : true, "allowEdgeOverflow" : false});
        }
        {
            var Q0;
            Q0=qCreatedBy(makeId("Top.planeOp"),FACE);
            var sketch = newSketch(context, id + "F14", { "sketchPlane" : qUnion([Q0])});
            skLineSegment(sketch, "E49.bottom", {"start": v(-5.4, 16.07) * mm, "end": v(4.6, 16.07) * mm});
            skLineSegment(sketch, "E49.top", {"start": v(-5.4, -21.93) * mm, "end": v(4.6, -21.93) * mm});
            skLineSegment(sketch, "E49.left", {"start": v(-7.4, 14.07) * mm, "end": v(-7.4, -19.93) * mm});
            skLineSegment(sketch, "E49.right", {"start": v(6.6, 14.07) * mm, "end": v(6.6, -19.93) * mm});
            skPoint(sketch, "E50.visualSharp", {"position": v(-7.4, 16.07) * mm});
            skArc(sketch, "E50.filletArc", {"start": v(-5.4, 16.07) * mm, "mid": v(-6.82, 15.49) * mm, "end": v(-7.4, 14.07) * mm});
            skPoint(sketch, "E51.visualSharp", {"position": v(-7.4, -21.93) * mm});
            skArc(sketch, "E51.filletArc", {"start": v(-7.4, -19.93) * mm, "mid": v(-6.82, -21.34) * mm, "end": v(-5.4, -21.93) * mm});
            skPoint(sketch, "E52.visualSharp", {"position": v(6.6, -21.93) * mm});
            skArc(sketch, "E52.filletArc", {"start": v(4.6, -21.93) * mm, "mid": v(6, -21.34) * mm, "end": v(6.6, -19.93) * mm});
            skPoint(sketch, "E53.visualSharp", {"position": v(6.6, 16.07) * mm});
            skArc(sketch, "E53.filletArc", {"start": v(6.6, 14.07) * mm, "mid": v(6, 15.49) * mm, "end": v(4.6, 16.07) * mm});
            skArc(sketch, "E54.0", {"start": v(-5.4, 17.07) * mm, "mid": v(-7.53, 16.2) * mm, "end": v(-8.4, 14.07) * mm});
            skLineSegment(sketch, "E54.1", {"start": v(-5.4, 17.07) * mm, "end": v(4.6, 17.07) * mm});
            skLineSegment(sketch, "E54.2", {"start": v(-8.4, 14.07) * mm, "end": v(-8.4, -19.93) * mm});
            skArc(sketch, "E54.3", {"start": v(7.6, 14.07) * mm, "mid": v(6.71, 16.2) * mm, "end": v(4.6, 17.07) * mm});
            skArc(sketch, "E54.4", {"start": v(-8.4, -19.93) * mm, "mid": v(-7.53, -22.05) * mm, "end": v(-5.4, -22.93) * mm});
            skLineSegment(sketch, "E54.5", {"start": v(-5.4, -22.93) * mm, "end": v(4.6, -22.93) * mm});
            skArc(sketch, "E54.6", {"start": v(4.6, -22.93) * mm, "mid": v(6.71, -22.05) * mm, "end": v(7.6, -19.93) * mm});
            skLineSegment(sketch, "E54.7", {"start": v(7.6, 14.07) * mm, "end": v(7.6, -19.93) * mm});
            skLineSegment(sketch, "E55", {"start": v(-0.4, 16.07) * mm, "end": v(-0.4, -21.93) * mm});
            skLineSegment(sketch, "E56.0", {"start": v(-0.9, 16.07) * mm, "end": v(-0.9, -21.93) * mm});
            skLineSegment(sketch, "E57.MirrorCS", {"start": v(0.1, 16.07) * mm, "end": v(0.1, -21.93) * mm});
            skLineSegment(sketch, "E58", {"start": v(0.1, 16.07) * mm, "end": v(4.6, 16.07) * mm, "construction": true});
            skLineSegment(sketch, "E59", {"start": v(2.34, 16.07) * mm, "end": v(2.34, 17.07) * mm});
            skLineSegment(sketch, "E60.0", {"start": v(2.84, 16.07) * mm, "end": v(2.84, 18.07) * mm});
            skLineSegment(sketch, "E61.MirrorCS", {"start": v(1.84, 16.07) * mm, "end": v(1.84, 18.07) * mm});
            skLineSegment(sketch, "E62.MirrorCS", {"start": v(-2.66, 16.07) * mm, "end": v(-2.66, 18.07) * mm});
            skLineSegment(sketch, "E63.MirrorCS", {"start": v(-3.66, 16.07) * mm, "end": v(-3.66, 18.07) * mm});
            skSolve(sketch);
        }
        {
            var Q0;
            Q0=makeQuery(id+"F14.imprint","IMPRINT",FACE,{"disambiguationData":[TD([[makeQuery(id+"F14.imprint","IMPRINT",EDGE,{"derivedFrom":sQuery(id+"F14.wireOp",EDGE,"E49.left")}),-1.0]])]});
            var Q1;
            {var subQ0=sQuery(id+"F14.wireOp",EDGE,"E49.bottom");var subQ10=makeQuery(id+"F14.imprint","INTERSECT",VERTEX,{"derivedFrom":[subQ0,sQuery(id+"F14.wireOp",EDGE,"E56.0")]});Q1=makeQuery(id+"F14.imprint","IMPRINT",FACE,{"disambiguationData":[TD([[makeQuery(id+"F14.imprint","IMPRINT",EDGE,{"disambiguationData":[TD([[subQ10,1.0]])],"derivedFrom":subQ0}),1.0]])]});}
            var Q2;
            {var subQ0=sQuery(id+"F14.wireOp",EDGE,"E55");Q2=makeQuery(id+"F14.imprint","IMPRINT",FACE,{"disambiguationData":[TD([[makeQuery(id+"F14.imprint","IMPRINT",EDGE,{"derivedFrom":subQ0}),-1.0]])]});}
            var Q3;
            {var subQ0=sQuery(id+"F14.wireOp",EDGE,"E55");Q3=makeQuery(id+"F14.imprint","IMPRINT",FACE,{"disambiguationData":[TD([[makeQuery(id+"F14.imprint","IMPRINT",EDGE,{"derivedFrom":subQ0}),1.0]])]});}
            extrude(context, id + "F15", {"entities" : qUnion([Q0, Q1, Q2, Q3]), "depth" : 25 * mm, "offsetDistance" : 25 * mm});
        }
        {
            var Q0;
            Q0=makeQuery(id+"F15.opExtrude","CAP_FACE",FACE,{"disambiguationData":[OSD([sQuery(id+"F14.wireOp",EDGE,"E49.bottom"),sQuery(id+"F14.wireOp",EDGE,"E49.top"),sQuery(id+"F14.wireOp",EDGE,"E49.left"),sQuery(id+"F14.wireOp",EDGE,"E49.right"),sQuery(id+"F14.wireOp",EDGE,"E50.filletArc"),sQuery(id+"F14.wireOp",EDGE,"E51.filletArc"),sQuery(id+"F14.wireOp",EDGE,"E52.filletArc"),sQuery(id+"F14.wireOp",EDGE,"E53.filletArc"),sQuery(id+"F14.wireOp",EDGE,"E54.0"),sQuery(id+"F14.wireOp",EDGE,"E54.1"),sQuery(id+"F14.wireOp",EDGE,"E54.2"),sQuery(id+"F14.wireOp",EDGE,"E54.3"),sQuery(id+"F14.wireOp",EDGE,"E54.4"),sQuery(id+"F14.wireOp",EDGE,"E54.5"),sQuery(id+"F14.wireOp",EDGE,"E54.6"),sQuery(id+"F14.wireOp",EDGE,"E54.7"),sQuery(id+"F14.wireOp",EDGE,"E56.0"),sQuery(id+"F14.wireOp",EDGE,"E57.MirrorCS"),sQuery(id+"F14.wireOp",EDGE,"E60.0"),sQuery(id+"F14.wireOp",EDGE,"E61.MirrorCS"),sQuery(id+"F14.wireOp",EDGE,"E62.MirrorCS"),sQuery(id+"F14.wireOp",EDGE,"E63.MirrorCS")])],"isStart":false});
            var Q1;
            Q1=makeQuery(id+"F15.opExtrude","CAP_FACE",FACE,{"disambiguationData":[OSD([sQuery(id+"F14.wireOp",EDGE,"E49.bottom"),sQuery(id+"F14.wireOp",EDGE,"E49.top"),sQuery(id+"F14.wireOp",EDGE,"E49.left"),sQuery(id+"F14.wireOp",EDGE,"E49.right"),sQuery(id+"F14.wireOp",EDGE,"E50.filletArc"),sQuery(id+"F14.wireOp",EDGE,"E51.filletArc"),sQuery(id+"F14.wireOp",EDGE,"E52.filletArc"),sQuery(id+"F14.wireOp",EDGE,"E53.filletArc"),sQuery(id+"F14.wireOp",EDGE,"E54.0"),sQuery(id+"F14.wireOp",EDGE,"E54.1"),sQuery(id+"F14.wireOp",EDGE,"E54.2"),sQuery(id+"F14.wireOp",EDGE,"E54.3"),sQuery(id+"F14.wireOp",EDGE,"E54.4"),sQuery(id+"F14.wireOp",EDGE,"E54.5"),sQuery(id+"F14.wireOp",EDGE,"E54.6"),sQuery(id+"F14.wireOp",EDGE,"E54.7"),sQuery(id+"F14.wireOp",EDGE,"E56.0"),sQuery(id+"F14.wireOp",EDGE,"E57.MirrorCS"),sQuery(id+"F14.wireOp",EDGE,"E60.0"),sQuery(id+"F14.wireOp",EDGE,"E61.MirrorCS"),sQuery(id+"F14.wireOp",EDGE,"E62.MirrorCS"),sQuery(id+"F14.wireOp",EDGE,"E63.MirrorCS")])],"isStart":true});
            var Q2;
            Q2=makeQuery(id+"F15.opExtrude","SWEPT_EDGE",EDGE,{"disambiguationData":[OSD([sQuery(id+"F14.wireOp",EDGE,"E49.bottom"),sQuery(id+"F14.wireOp",EDGE,"E56.0")])]});
            var Q3;
            Q3=makeQuery(id+"F15.opExtrude","SWEPT_EDGE",EDGE,{"disambiguationData":[OSD([sQuery(id+"F14.wireOp",EDGE,"E49.bottom"),sQuery(id+"F14.wireOp",EDGE,"E57.MirrorCS")])]});
            var Q4;
            Q4=makeQuery(id+"F15.opExtrude","SWEPT_EDGE",EDGE,{"disambiguationData":[OSD([sQuery(id+"F14.wireOp",EDGE,"E49.top"),sQuery(id+"F14.wireOp",EDGE,"E56.0")])]});
            var Q5;
            Q5=makeQuery(id+"F15.opExtrude","SWEPT_EDGE",EDGE,{"disambiguationData":[OSD([sQuery(id+"F14.wireOp",EDGE,"E49.top"),sQuery(id+"F14.wireOp",EDGE,"E57.MirrorCS")])]});
            fillet(context, id + "F16", {"entities" : qUnion([Q0, Q1, Q2, Q3, Q4, Q5]), "radius" : 0.5 * mm, "tangentPropagation" : true, "allowEdgeOverflow" : false});
        }
    });
